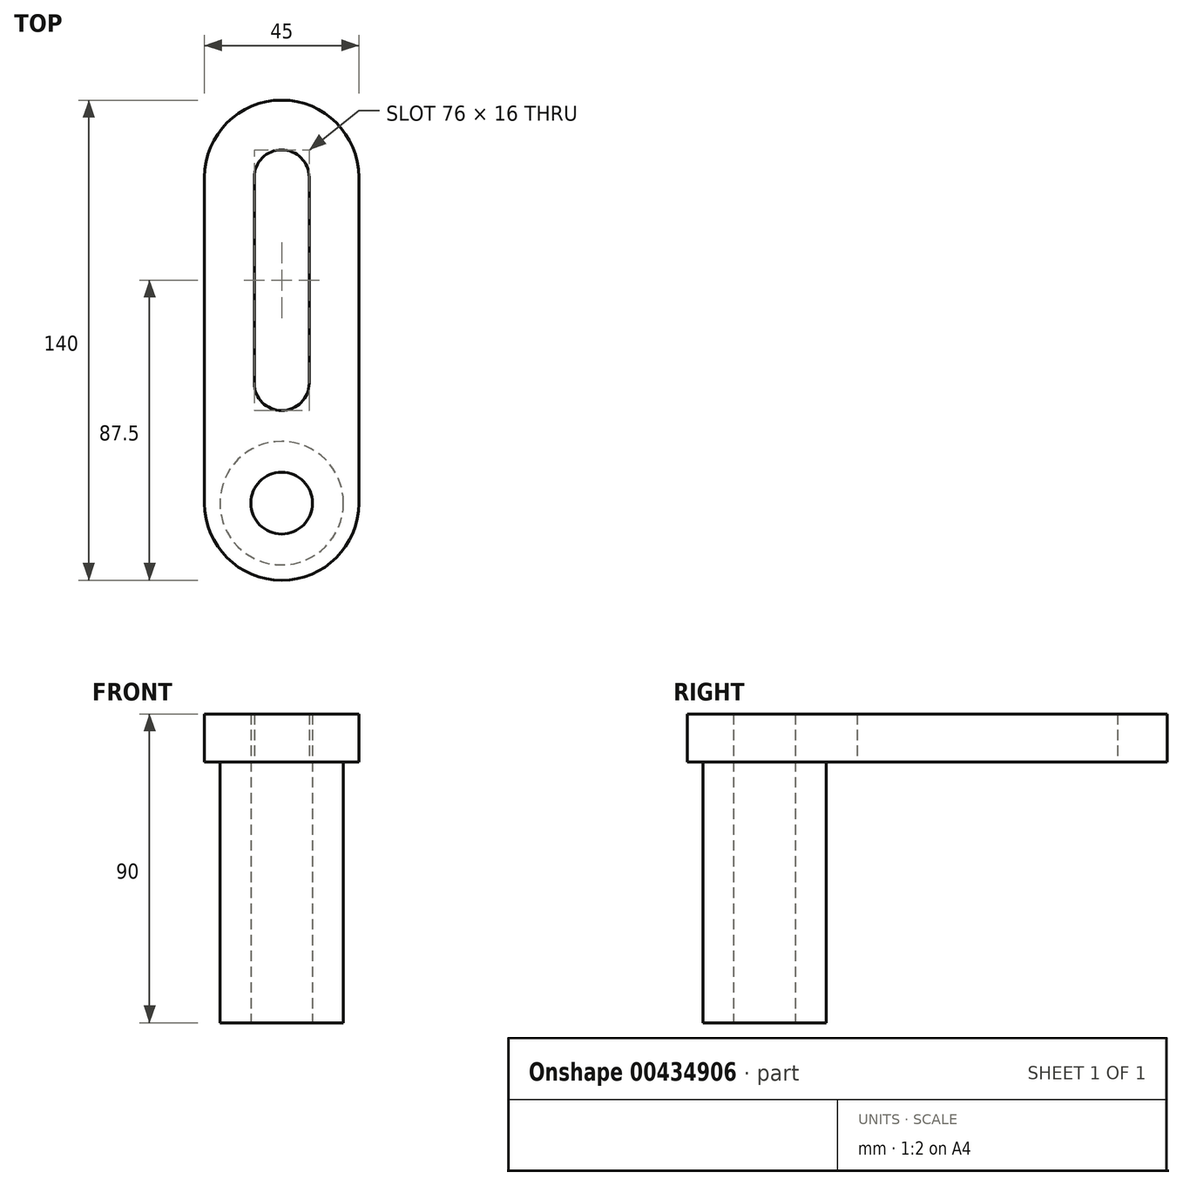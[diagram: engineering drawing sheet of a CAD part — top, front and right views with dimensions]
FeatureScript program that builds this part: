
annotation { "Feature Type Name" : "Feature", "Feature Type Description" : "" }
export const myFeature = defineFeature(function(context is Context, id is Id, definition is map)
    precondition{}
    {
        {
            var Q0;
            Q0=qCreatedBy(makeId("Top.planeOp"),FACE);
            var sketch = newSketch(context, id + "F0", { "sketchPlane" : qUnion([Q0])});
            skLineSegment(sketch, "E0.left", {"start": v(-5.81, 56.1) * mm, "end": v(-5.81, -38.9) * mm});
            skLineSegment(sketch, "E0.right", {"start": v(-50.81, 56.1) * mm, "end": v(-50.81, -38.9) * mm});
            skArc(sketch, "E1", {"start": v(-5.81, -38.9) * mm, "mid": v(-28.31, -61.4) * mm, "end": v(-50.81, -38.9) * mm});
            skArc(sketch, "E2", {"start": v(-5.81, 56.1) * mm, "mid": v(-28.31, 78.6) * mm, "end": v(-50.81, 56.1) * mm});
            skCircle(sketch, "E3", {"center": v(-28.31, -38.9) * mm, "radius": 18 * mm});
            skCircle(sketch, "E4", {"center": v(-28.31, -38.9) * mm, "radius": 9 * mm});
            skLineSegment(sketch, "E5", {"start": v(-36.31, 56.1) * mm, "end": v(-36.31, -3.9) * mm});
            skLineSegment(sketch, "E6", {"start": v(-20.31, -3.9) * mm, "end": v(-20.31, 56.1) * mm});
            skPoint(sketch, "E7.start.orphan", {"position": v(-28.31, -3.9) * mm});
            skArc(sketch, "E8", {"start": v(-36.31, -3.9) * mm, "mid": v(-28.31, -11.9) * mm, "end": v(-20.31, -3.9) * mm});
            skArc(sketch, "E9", {"start": v(-36.31, 56.1) * mm, "mid": v(-28.31, 64.1) * mm, "end": v(-20.31, 56.1) * mm});
            skSolve(sketch);
        }
        {
            var Q0;
            Q0=makeQuery(id+"F0.imprint","IMPRINT",FACE,{"disambiguationData":[TD([[makeQuery(id+"F0.imprint","IMPRINT",EDGE,{"derivedFrom":sQuery(id+"F0.wireOp",EDGE,"E0.left")}),-1.0]])]});
            var Q1;
            Q1=makeQuery(id+"F0.imprint","IMPRINT",FACE,{"disambiguationData":[TD([[makeQuery(id+"F0.imprint","IMPRINT",EDGE,{"derivedFrom":sQuery(id+"F0.wireOp",EDGE,"E3")}),1.0]])]});
            extrude(context, id + "F1", {"entities" : qUnion([Q0, Q1]), "depth" : 14 * mm});
        }
        {
            var Q0;
            Q0=makeQuery(id+"F0.imprint","IMPRINT",FACE,{"disambiguationData":[TD([[makeQuery(id+"F0.imprint","IMPRINT",EDGE,{"derivedFrom":sQuery(id+"F0.wireOp",EDGE,"E3")}),1.0]])]});
            extrude(context, id + "F2", {"entities" : qUnion([Q0]), "operationType" : NewBodyOperationType.ADD, "oppositeDirection" : true, "depth" : 76 * mm});
        }
    });
